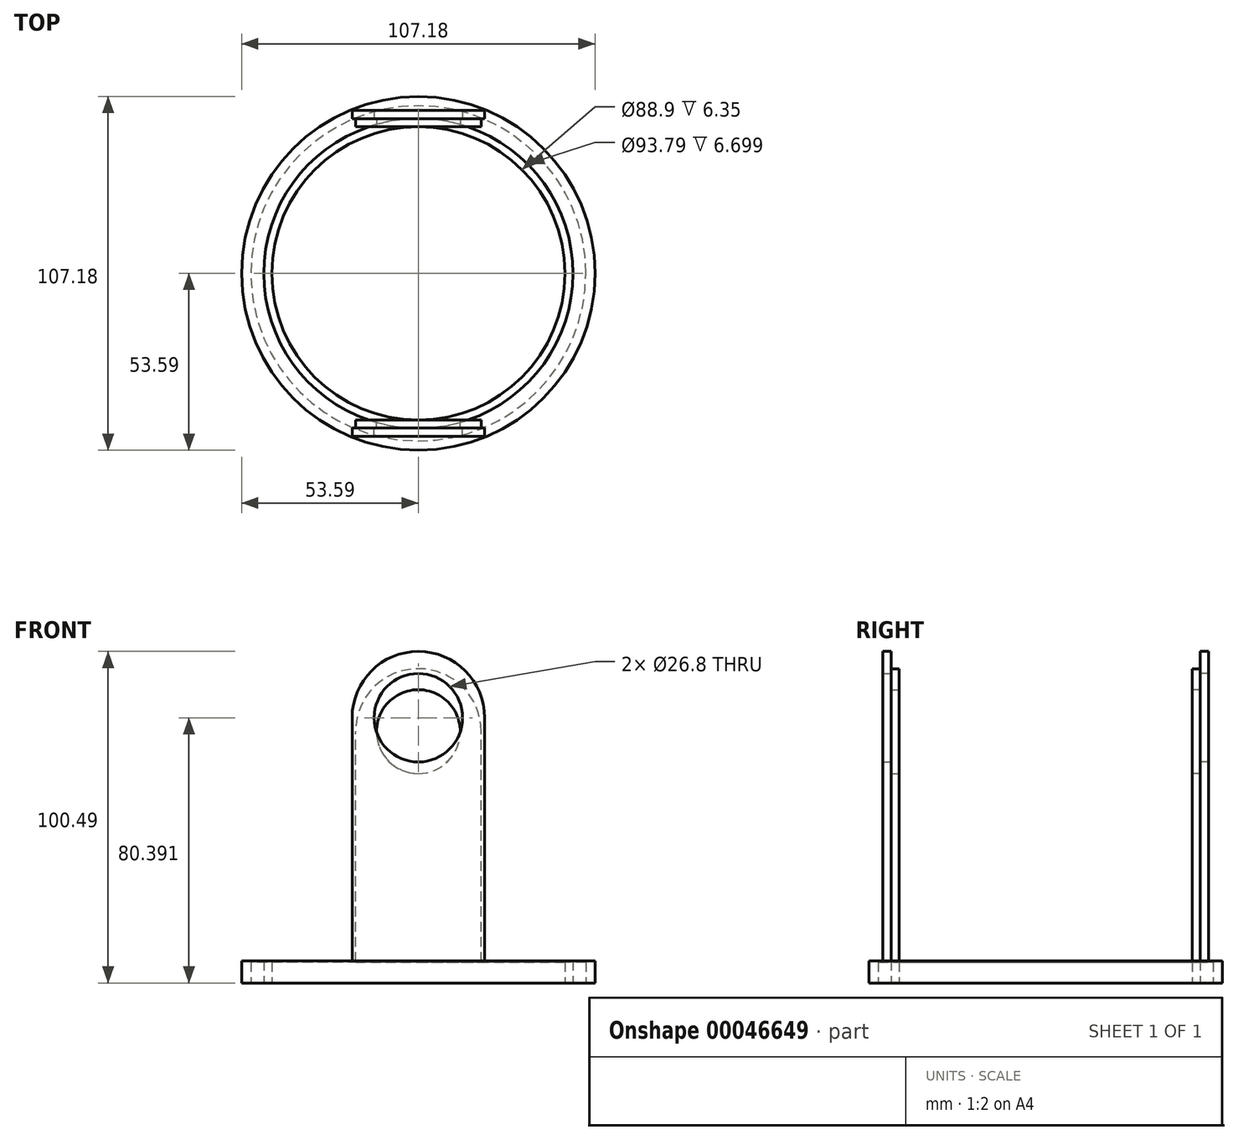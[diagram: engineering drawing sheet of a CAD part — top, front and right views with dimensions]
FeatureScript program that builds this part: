
annotation { "Feature Type Name" : "Feature", "Feature Type Description" : "" }
export const myFeature = defineFeature(function(context is Context, id is Id, definition is map)
    precondition{}
    {
        {
            var Q0;
            Q0=qCreatedBy(makeId("Top.planeOp"),FACE);
            var sketch = newSketch(context, id + "F0", { "sketchPlane" : qUnion([Q0])});
            skCircle(sketch, "E0", {"center": v(0, 0) * mm, "radius": 50.8 * mm});
            skCircle(sketch, "E1", {"center": v(0, 0) * mm, "radius": 44.45 * mm});
            skSolve(sketch);
        }
        {
            var Q0;
            Q0=makeQuery(id+"F0.imprint","IMPRINT",FACE,{"disambiguationData":[TD([[makeQuery(id+"F0.imprint","IMPRINT",EDGE,{"derivedFrom":sQuery(id+"F0.wireOp",EDGE,"E0")}),1.0]])]});
            extrude(context, id + "F1", {"entities" : qUnion([Q0]), "depth" : 6.35 * mm});
        }
        {
            var Q0;
            Q0=qCreatedBy(makeId("Front.planeOp"),FACE);
            cPlane(context, id + "F2", {"entities" : qUnion([Q0]), "cplaneType" : CPlaneType.OFFSET, "offset" : 44.45 * mm, "width" : 152.4 * mm, "height" : 152.4 * mm});
        }
        {
            var Q0;
            Q0=qCreatedBy(id+"F2.planeOp",FACE);
            var sketch = newSketch(context, id + "F3", { "sketchPlane" : qUnion([Q0])});
            skLineSegment(sketch, "E2.bottom", {"start": v(-19.05, 0) * mm, "end": v(19.05, 0) * mm});
            skLineSegment(sketch, "E2.top", {"start": v(-19.05, 88.9) * mm, "end": v(19.05, 88.9) * mm});
            skLineSegment(sketch, "E2.left", {"start": v(-19.05, 0) * mm, "end": v(-19.05, 88.9) * mm});
            skLineSegment(sketch, "E2.right", {"start": v(19.05, 0) * mm, "end": v(19.05, 88.9) * mm});
            skCircle(sketch, "E3", {"center": v(0, 76.2) * mm, "radius": 12.7 * mm});
            skCircle(sketch, "E4", {"center": v(0, 76.2) * mm, "radius": 19.05 * mm});
            skSolve(sketch);
        }
        {
            var Q0;
            {var subQ3=sQuery(id+"F3.wireOp",EDGE,"E2.bottom");Q0=makeQuery(id+"F3.imprint","IMPRINT",FACE,{"disambiguationData":[TD([[makeQuery(id+"F3.imprint","IMPRINT",EDGE,{"derivedFrom":subQ3}),1.0]])]});}
            var Q1;
            {var subQ5=sQuery(id+"F3.wireOp",EDGE,"E3");Q1=makeQuery(id+"F3.imprint","IMPRINT",FACE,{"disambiguationData":[TD([[makeQuery(id+"F3.imprint","IMPRINT",EDGE,{"derivedFrom":subQ5}),-1.0]])]});}
            var Q2;
            {var subQ0=sQuery(id+"F3.wireOp",EDGE,"E4");var subQ1=sQuery(id+"F3.wireOp",EDGE,"E2.top");var subQ3=makeQuery(id+"F3.imprint","INTERSECT",VERTEX,{"disambiguationData":[OD(0.0)],"derivedFrom":[subQ1,subQ0]});Q2=makeQuery(id+"F3.imprint","IMPRINT",FACE,{"disambiguationData":[TD([[makeQuery(id+"F3.imprint","IMPRINT",EDGE,{"disambiguationData":[TD([[subQ3,-1.0]])],"derivedFrom":subQ1}),1.0]])]});}
            extrude(context, id + "F4", {"entities" : qUnion([Q0, Q1, Q2]), "operationType" : NewBodyOperationType.ADD, "depth" : 2.38 * mm});
        }
        {
            var Q0;
            Q0=makeQuery(id+"F1.opExtrude","SWEPT_BODY",BODY,{"disambiguationData":[OSD([sQuery(id+"F0.wireOp",EDGE,"E0"),sQuery(id+"F0.wireOp",EDGE,"E1")])]});
            var Q1;
            Q1=qCreatedBy(makeId("Front.planeOp"),FACE);
            mirror(context, id + "F5", {"operationType" : NewBodyOperationType.ADD, "entities" : qUnion([Q0]), "mirrorPlane" : qUnion([Q1])});
        }
        {
            var Q0;
            Q0=makeQuery(id+"F1.opExtrude","SWEPT_BODY",BODY,{"disambiguationData":[OSD([sQuery(id+"F0.wireOp",EDGE,"E0"),sQuery(id+"F0.wireOp",EDGE,"E1")])]});
            var Q1;
            Q1=qCreatedBy(makeId("Origin.pointOp"),VERTEX);
            transform(context, id + "F6", {"entities" : qUnion([Q0]), "transformType" : TransformType.SCALE_UNIFORMLY, "scale" : 1.05, "makeCopy" : true, "scalePoint" : qUnion([Q1])});
        }
    });
